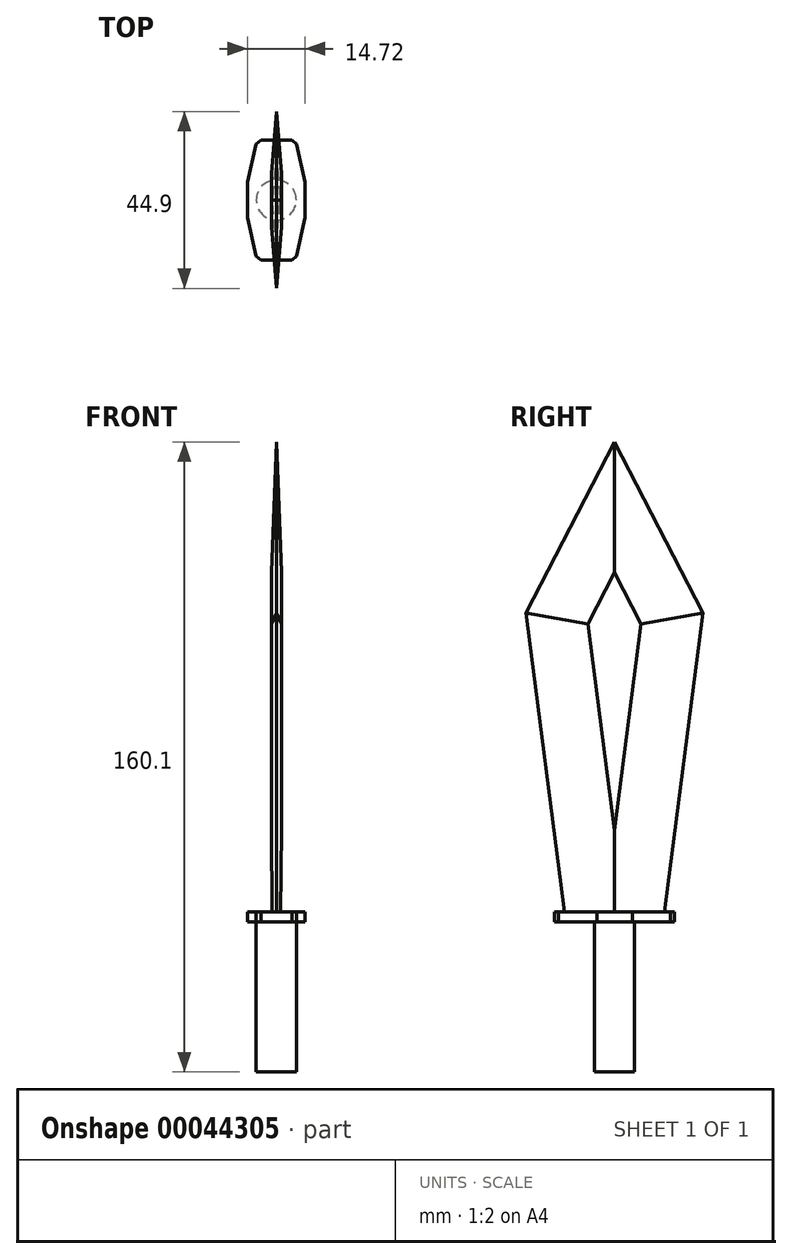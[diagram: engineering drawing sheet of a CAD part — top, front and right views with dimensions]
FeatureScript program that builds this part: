
annotation { "Feature Type Name" : "Feature", "Feature Type Description" : "" }
export const myFeature = defineFeature(function(context is Context, id is Id, definition is map)
    precondition{}
    {
        {
            var Q0;
            Q0=qCreatedBy(makeId("Right.planeOp"),FACE);
            var sketch = newSketch(context, id + "F0", { "sketchPlane" : qUnion([Q0])});
            skLineSegment(sketch, "E0", {"start": v(0, 0) * mm, "end": v(-12.7, 0) * mm});
            skLineSegment(sketch, "E1", {"start": v(-12.7, 0) * mm, "end": v(0, 0) * mm});
            skLineSegment(sketch, "E2", {"start": v(0, 0) * mm, "end": v(0, 15.27) * mm});
            skLineSegment(sketch, "E3.MirrorCS", {"start": v(12.7, 0) * mm, "end": v(0, 0) * mm});
            skLineSegment(sketch, "E4", {"start": v(-12.7, 0) * mm, "end": v(-22.45, 75.98) * mm});
            skLineSegment(sketch, "E5", {"start": v(-22.45, 75.98) * mm, "end": v(0, 119.46) * mm});
            skLineSegment(sketch, "E6.MirrorCS", {"start": v(12.7, 0) * mm, "end": v(22.45, 75.98) * mm});
            skLineSegment(sketch, "E7.MirrorCS", {"start": v(22.45, 75.98) * mm, "end": v(0, 119.46) * mm});
            skSolve(sketch);
        }
        {
            var Q0;
            Q0 = qSketchRegion(id + "F0", true);
            extrude(context, id + "F1", {"entities" : qUnion([Q0]), "endBound" : BoundingType.SYMMETRIC, "depth" : 2.54 * mm});
        }
        {
            var Q0;
            Q0=makeQuery(id+"F1.opExtrude","CAP_EDGE",EDGE,{"disambiguationData":[OSD([sQuery(id+"F0.wireOp",EDGE,"E7.MirrorCS")])],"isStart":false});
            var Q1;
            Q1=makeQuery(id+"F1.opExtrude","CAP_EDGE",EDGE,{"disambiguationData":[OSD([sQuery(id+"F0.wireOp",EDGE,"E5")])],"isStart":false});
            var Q2;
            Q2=makeQuery(id+"F1.opExtrude","CAP_EDGE",EDGE,{"disambiguationData":[OSD([sQuery(id+"F0.wireOp",EDGE,"E4")])],"isStart":false});
            var Q3;
            Q3=makeQuery(id+"F1.opExtrude","CAP_EDGE",EDGE,{"disambiguationData":[OSD([sQuery(id+"F0.wireOp",EDGE,"E6.MirrorCS")])],"isStart":false});
            chamfer(context, id + "F2", {"entities" : qUnion([Q0, Q1, Q2, Q3]), "chamferType" : ChamferType.TWO_OFFSETS, "width1" : 15.24 * mm, "oppositeDirection" : false, "width2" : 1.27 * mm, "tangentPropagation" : true});
        }
        {
            var Q0;
            Q0=makeQuery(id+"F1.opExtrude","CAP_EDGE",EDGE,{"disambiguationData":[OSD([sQuery(id+"F0.wireOp",EDGE,"E6.MirrorCS")])],"isStart":true});
            var Q1;
            Q1=makeQuery(id+"F1.opExtrude","CAP_EDGE",EDGE,{"disambiguationData":[OSD([sQuery(id+"F0.wireOp",EDGE,"E7.MirrorCS")])],"isStart":true});
            var Q2;
            Q2=makeQuery(id+"F1.opExtrude","CAP_EDGE",EDGE,{"disambiguationData":[OSD([sQuery(id+"F0.wireOp",EDGE,"E5")])],"isStart":true});
            chamfer(context, id + "F3", {"entities" : qUnion([Q0, Q1, Q2]), "chamferType" : ChamferType.TWO_OFFSETS, "width1" : 1.27 * mm, "oppositeDirection" : false, "width2" : 15.24 * mm, "tangentPropagation" : true});
        }
        {
            var Q0;
            Q0=makeQuery(id+"F1.opExtrude","CAP_EDGE",EDGE,{"disambiguationData":[OSD([sQuery(id+"F0.wireOp",EDGE,"E4")])],"isStart":true});
            chamfer(context, id + "F4", {"entities" : qUnion([Q0]), "chamferType" : ChamferType.TWO_OFFSETS, "width1" : 15.24 * mm, "oppositeDirection" : false, "width2" : 1.27 * mm, "tangentPropagation" : true});
        }
        {
            var Q0;
            Q0=makeQuery(id+"F1.opExtrude","SWEPT_FACE",FACE,{"disambiguationData":[OSD([sQuery(id+"F0.wireOp",EDGE,"E1"),sQuery(id+"F0.wireOp",EDGE,"E3.MirrorCS")])]});
            var sketch = newSketch(context, id + "F5", { "sketchPlane" : qUnion([Q0])});
            skPoint(sketch, "E8.0.midPoint", {"position": v(0, 12.7) * mm});
            skLineSegment(sketch, "E9", {"start": v(0, 12.7) * mm, "end": v(0, 15.24) * mm});
            skLineSegment(sketch, "E10.0", {"start": v(-4.95, 15.24) * mm, "end": v(4.95, 15.24) * mm});
            skLineSegment(sketch, "E10.1", {"start": v(4.95, 15.24) * mm, "end": v(12.96, 9.42) * mm});
            skLineSegment(sketch, "E10.2", {"start": v(12.96, 9.42) * mm, "end": v(16.02, 0) * mm});
            skLineSegment(sketch, "E10.3", {"start": v(16.02, 0) * mm, "end": v(12.96, -9.42) * mm});
            skLineSegment(sketch, "E10.4", {"start": v(12.96, -9.42) * mm, "end": v(4.95, -15.24) * mm});
            skLineSegment(sketch, "E10.5", {"start": v(4.95, -15.24) * mm, "end": v(-4.95, -15.24) * mm});
            skLineSegment(sketch, "E10.6", {"start": v(-4.95, -15.24) * mm, "end": v(-12.96, -9.42) * mm});
            skLineSegment(sketch, "E10.7", {"start": v(-12.96, -9.42) * mm, "end": v(-16.02, 0) * mm});
            skLineSegment(sketch, "E10.8", {"start": v(-16.02, 0) * mm, "end": v(-12.96, 9.42) * mm});
            skLineSegment(sketch, "E10.9", {"start": v(-12.96, 9.42) * mm, "end": v(-4.95, 15.24) * mm});
            skPoint(sketch, "E10.0.midPoint", {"position": v(0, 15.24) * mm});
            skLineSegment(sketch, "E11", {"start": v(-4.95, 15.24) * mm, "end": v(-7.36, 4.5) * mm});
            skLineSegment(sketch, "E12", {"start": v(-7.36, 4.5) * mm, "end": v(-7.36, 0) * mm});
            skLineSegment(sketch, "E13", {"start": v(-7.36, 0) * mm, "end": v(0, 0) * mm});
            skLineSegment(sketch, "E14.MirrorCS", {"start": v(-7.36, -4.5) * mm, "end": v(-7.36, 0) * mm});
            skLineSegment(sketch, "E15.MirrorCS", {"start": v(-4.95, -15.24) * mm, "end": v(-7.36, -4.5) * mm});
            skLineSegment(sketch, "E16.MirrorCS", {"start": v(4.95, 15.24) * mm, "end": v(7.36, 4.5) * mm});
            skLineSegment(sketch, "E17.MirrorCS", {"start": v(7.36, -4.5) * mm, "end": v(7.36, 0) * mm});
            skLineSegment(sketch, "E18.MirrorCS", {"start": v(7.36, 4.5) * mm, "end": v(7.36, 0) * mm});
            skLineSegment(sketch, "E19.MirrorCS", {"start": v(4.95, -15.24) * mm, "end": v(7.36, -4.5) * mm});
            skSolve(sketch);
        }
        {
            var Q0;
            {var subQ0=sQuery(id+"F0.wireOp",EDGE,"E4");var subQ1=makeQuery(id+"F1.opExtrude","SWEPT_FACE",FACE,{"disambiguationData":[OSD([sQuery(id+"F0.wireOp",EDGE,"E1"),sQuery(id+"F0.wireOp",EDGE,"E3.MirrorCS")])]});Q0=makeQuery(id+"F5.imprint","IMPRINT",FACE,{"disambiguationData":[TD([[makeQuery(id+"F5.imprint","IMPRINT",EDGE,{"derivedFrom":makeQuery(id+"F2.opChamfer","BLEND_EDGE",EDGE,{"blendedFrom":[makeQuery(id+"F1.opExtrude","CAP_EDGE",EDGE,{"disambiguationData":[OSD([subQ0])],"isStart":false}),subQ1],"blendedInto":[subQ1]})}),1.0]])]});}
            var Q1;
            {var subQ4=sQuery(id+"F5.wireOp",EDGE,"E9");Q1=makeQuery(id+"F5.imprint","IMPRINT",FACE,{"disambiguationData":[TD([[makeQuery(id+"F5.imprint","IMPRINT",EDGE,{"derivedFrom":subQ4}),1.0]])]});}
            var Q2;
            {var subQ7=sQuery(id+"F5.wireOp",EDGE,"E9");Q2=makeQuery(id+"F5.imprint","IMPRINT",FACE,{"disambiguationData":[TD([[makeQuery(id+"F5.imprint","IMPRINT",EDGE,{"derivedFrom":subQ7}),-1.0]])]});}
            var Q3;
            {var subQ0=sQuery(id+"F0.wireOp",EDGE,"E4");var subQ1=makeQuery(id+"F1.opExtrude","SWEPT_FACE",FACE,{"disambiguationData":[OSD([sQuery(id+"F0.wireOp",EDGE,"E1"),sQuery(id+"F0.wireOp",EDGE,"E3.MirrorCS")])]});Q3=makeQuery(id+"F5.imprint","IMPRINT",FACE,{"disambiguationData":[TD([[makeQuery(id+"F5.imprint","IMPRINT",EDGE,{"derivedFrom":makeQuery(id+"F2.opChamfer","BLEND_EDGE",EDGE,{"blendedFrom":[makeQuery(id+"F1.opExtrude","CAP_EDGE",EDGE,{"disambiguationData":[OSD([subQ0])],"isStart":false}),subQ1],"blendedInto":[subQ1]})}),1.0]])]});}
            extrude(context, id + "F6", {"entities" : qUnion([Q0, Q1, Q2, Q3]), "depth" : 2.54 * mm});
        }
        {
            var Q0;
            Q0=makeQuery(id+"F6.opExtrude","SWEPT_EDGE",EDGE,{"disambiguationData":[OSD([sQuery(id+"F5.wireOp",EDGE,"E10.4"),sQuery(id+"F5.wireOp",EDGE,"E10.5"),sQuery(id+"F5.wireOp",EDGE,"E19.MirrorCS")])]});
            var Q1;
            Q1=makeQuery(id+"F6.opExtrude","SWEPT_EDGE",EDGE,{"disambiguationData":[OSD([sQuery(id+"F5.wireOp",EDGE,"E10.5"),sQuery(id+"F5.wireOp",EDGE,"E10.6"),sQuery(id+"F5.wireOp",EDGE,"E15.MirrorCS")])]});
            var Q2;
            Q2=makeQuery(id+"F6.opExtrude","SWEPT_EDGE",EDGE,{"disambiguationData":[OSD([sQuery(id+"F5.wireOp",EDGE,"E10.0"),sQuery(id+"F5.wireOp",EDGE,"E10.1"),sQuery(id+"F5.wireOp",EDGE,"E16.MirrorCS")])]});
            var Q3;
            Q3=makeQuery(id+"F6.opExtrude","SWEPT_EDGE",EDGE,{"disambiguationData":[OSD([sQuery(id+"F5.wireOp",EDGE,"E10.0"),sQuery(id+"F5.wireOp",EDGE,"E10.9"),sQuery(id+"F5.wireOp",EDGE,"E11")])]});
            chamfer(context, id + "F7", {"entities" : qUnion([Q0, Q1, Q2, Q3]), "width" : 1.27 * mm, "tangentPropagation" : true});
        }
        {
            var Q0;
            Q0=makeQuery(id+"F6.opExtrude","CAP_FACE",FACE,{"disambiguationData":[OSD([sQuery(id+"F5.wireOp",EDGE,"E10.0"),sQuery(id+"F5.wireOp",EDGE,"E10.5"),sQuery(id+"F5.wireOp",EDGE,"E11"),sQuery(id+"F5.wireOp",EDGE,"E12"),sQuery(id+"F5.wireOp",EDGE,"E14.MirrorCS"),sQuery(id+"F5.wireOp",EDGE,"E15.MirrorCS"),sQuery(id+"F5.wireOp",EDGE,"E16.MirrorCS"),sQuery(id+"F5.wireOp",EDGE,"E17.MirrorCS"),sQuery(id+"F5.wireOp",EDGE,"E18.MirrorCS"),sQuery(id+"F5.wireOp",EDGE,"E19.MirrorCS")])],"isStart":false});
            var sketch = newSketch(context, id + "F8", { "sketchPlane" : qUnion([Q0])});
            skCircle(sketch, "E20", {"center": v(0, 0) * mm, "radius": 5.08 * mm});
            skSolve(sketch);
        }
        {
            var Q0;
            Q0 = qSketchRegion(id + "F8", true);
            extrude(context, id + "F9", {"entities" : qUnion([Q0]), "depth" : 38.1 * mm});
        }
    });
